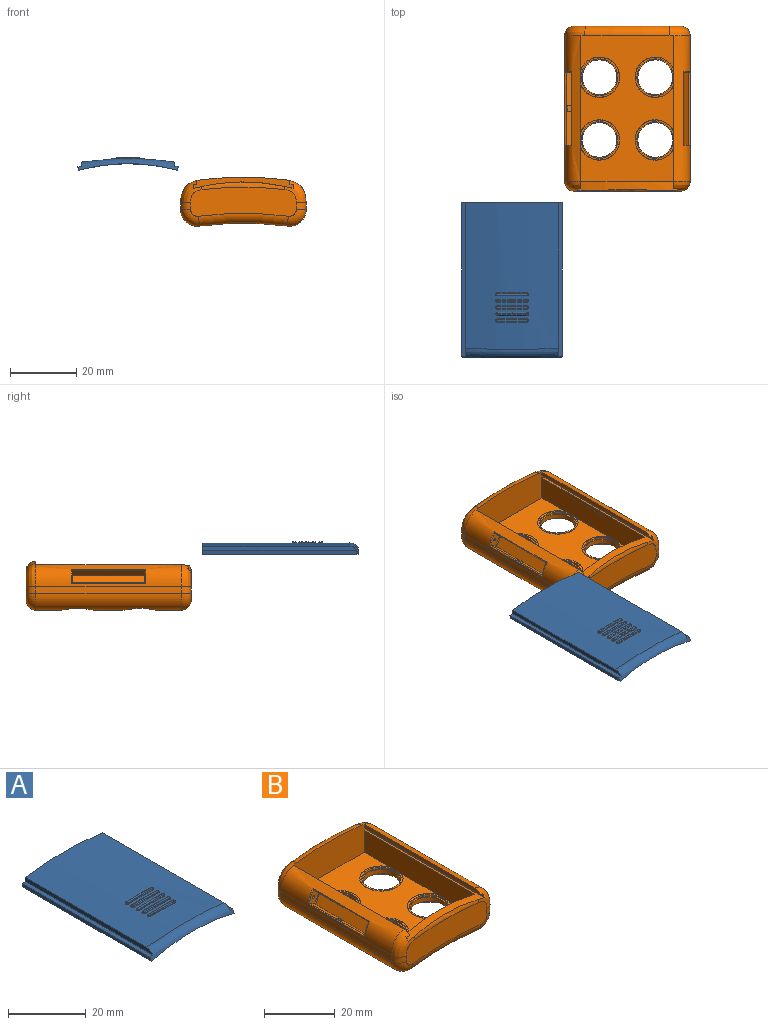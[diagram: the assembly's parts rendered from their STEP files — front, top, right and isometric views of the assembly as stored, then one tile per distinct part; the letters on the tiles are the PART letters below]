
ASSEMBLY  parts=2 mates=1
PART A: 107 faces, bbox 33.4x47.1x4.3 mm
  f0: plane 30.4x3.48mm, normal (0,1,0), area 31.7mm2, adj f1,f2,f3,f4,f5,f6,f7,f8
  f1: cylinder r=58.25mm len=47mm, axis (0,-1,0), area 297.3mm2, adj f0,f2,f8,f9,f10,f105,f106
  f2: plane 47.03x1.14mm, normal (0.99,0,-0.13), area 52.1mm2, adj f0,f1,f3,f9
  f3: plane 46.53x1.1mm, normal (0.13,0,0.99), area 51.7mm2, adj f0,f2,f4,f9
  f4: plane 46.64x1.34mm, normal (1,0,0), area 56.4mm2, adj f0,f3,f5,f9
  f5: cylinder r=99.82mm len=44.4mm, axis (0,-1,0), area 1204.5mm2, adj f0,f4,f6,f9,f13,f14,f15,f16
  f6: plane 46.64x1.35mm, normal (-1,0,0), area 56.4mm2, adj f0,f5,f7,f9
  f7: plane 46.53x1.1mm, normal (-0.13,0,0.99), area 51.7mm2, adj f0,f6,f8,f9
  f8: plane 47.03x1.13mm, normal (-0.99,0,-0.13), area 52.1mm2, adj f0,f1,f7,f9
  f9: bspline ~33.25x3.8mm, area 98.9mm2, adj f1,f2,f3,f4,f5,f6,f7,f8
  f10: plane 26.16x1.86mm, normal (0,1,0), area 19.6mm2, adj f1,f11,f105,f106
  f11: plane 43x20.61mm, normal (0,0,-1), area 886.4mm2, adj f0,f10,f105,f106
  f12: cylinder r=99.82mm len=9.62mm, axis (0,-1,0), area 5.7mm2, adj f95,f96,f97,f98,f99,f100,f101,f102
  f13: cylinder r=0.5mm len=0.1mm, axis (0,0,-1), area 0mm2, adj f5,f14,f21,f99
  f14: cylinder r=0.5mm len=0.1mm, axis (0,0,-1), area 0mm2, adj f5,f13,f15,f97
  f15: plane 4.46x0.2mm, normal (0,-1,0), area 0.4mm2, adj f5,f14,f16,f95
  f16: cylinder r=0.5mm len=1mm, axis (0,0,-1), area 0.2mm2, adj f5,f15,f17,f96
  f17: plane 4.46x0.2mm, normal (0,1,0), area 0.4mm2, adj f5,f16,f18,f98
  f18: cylinder r=0.5mm len=0.1mm, axis (0,0,-1), area 0mm2, adj f5,f17,f19,f100
  f19: cylinder r=0.5mm len=0.1mm, axis (0,0,-1), area 0mm2, adj f5,f18,f20,f102
  f20: plane 4.46x0.2mm, normal (0,1,0), area 0.4mm2, adj f5,f19,f22,f104
  f21: plane 4.46x0.2mm, normal (0,-1,0), area 0.4mm2, adj f5,f13,f22,f101
  f22: cylinder r=0.5mm len=1mm, axis (0,0,-1), area 0.2mm2, adj f5,f20,f21,f103
  f23: cylinder r=99.82mm len=9.56mm, axis (0,-1,0), area 5.7mm2, adj f85,f86,f87,f88,f89,f90,f91,f92
  f24: cylinder r=0.5mm len=0.1mm, axis (0,0,-1), area 0mm2, adj f5,f25,f32,f89
  f25: cylinder r=0.5mm len=0.1mm, axis (0,0,-1), area 0mm2, adj f5,f24,f26,f87
  f26: plane 4.46x0.2mm, normal (0,1,0), area 0.4mm2, adj f5,f25,f27,f85
  f27: cylinder r=0.5mm len=1mm, axis (0,0,-1), area 0.2mm2, adj f5,f26,f28,f86
  f28: plane 4.46x0.2mm, normal (0,-1,0), area 0.4mm2, adj f5,f27,f29,f88
  f29: cylinder r=0.5mm len=0.1mm, axis (0,0,-1), area 0mm2, adj f5,f28,f30,f90
  f30: cylinder r=0.5mm len=0.1mm, axis (0,0,-1), area 0mm2, adj f5,f29,f31,f92
  f31: plane 4.46x0.2mm, normal (0,-1,0), area 0.4mm2, adj f5,f30,f33,f94
  f32: plane 4.46x0.2mm, normal (0,1,0), area 0.4mm2, adj f5,f24,f33,f91
  f33: cylinder r=0.5mm len=1mm, axis (0,0,-1), area 0.2mm2, adj f5,f31,f32,f93
  f34: cylinder r=99.82mm len=8.93mm, axis (0,-1,0), area 5.4mm2, adj f61,f62,f63,f64
  f35: cylinder r=0.5mm len=1mm, axis (0,0,-1), area 0.2mm2, adj f5,f36,f37,f62
  f36: plane 8.92x0.2mm, normal (0,-1,0), area 0.9mm2, adj f5,f35,f38,f64
  f37: plane 8.92x0.2mm, normal (0,1,0), area 0.9mm2, adj f5,f35,f38,f61
  f38: cylinder r=0.5mm len=1mm, axis (0,0,-1), area 0.2mm2, adj f5,f36,f37,f63
  f39: cylinder r=99.82mm len=9.58mm, axis (0,-1,0), area 5.7mm2, adj f75,f76,f77,f78,f79,f80,f81,f82
  f40: cylinder r=0.5mm len=0.1mm, axis (0,0,-1), area 0mm2, adj f5,f41,f48,f79
  f41: cylinder r=0.5mm len=0.1mm, axis (0,0,-1), area 0mm2, adj f5,f40,f42,f77
  f42: plane 4.46x0.2mm, normal (0,1,0), area 0.4mm2, adj f5,f41,f43,f75
  f43: cylinder r=0.5mm len=1mm, axis (0,0,-1), area 0.2mm2, adj f5,f42,f44,f76
  f44: plane 4.46x0.2mm, normal (0,-1,0), area 0.4mm2, adj f5,f43,f45,f78
  f45: cylinder r=0.5mm len=0.1mm, axis (0,0,-1), area 0mm2, adj f5,f44,f46,f80
  f46: cylinder r=0.5mm len=0.1mm, axis (0,0,-1), area 0mm2, adj f5,f45,f47,f82
  f47: plane 4.46x0.2mm, normal (0,-1,0), area 0.4mm2, adj f5,f46,f49,f84
  f48: plane 4.46x0.2mm, normal (0,1,0), area 0.4mm2, adj f5,f40,f49,f81
  f49: cylinder r=0.5mm len=1mm, axis (0,0,-1), area 0.2mm2, adj f5,f47,f48,f83
  f50: cylinder r=99.82mm len=9.6mm, axis (0,-1,0), area 5.7mm2, adj f65,f66,f67,f68,f69,f70,f71,f72
  f51: cylinder r=0.5mm len=0.1mm, axis (0,0,-1), area 0mm2, adj f5,f52,f59,f69
  f52: cylinder r=0.5mm len=0.1mm, axis (0,0,-1), area 0mm2, adj f5,f51,f53,f67
  f53: plane 4.46x0.2mm, normal (0,1,0), area 0.4mm2, adj f5,f52,f54,f65
  f54: cylinder r=0.5mm len=1mm, axis (0,0,-1), area 0.2mm2, adj f5,f53,f55,f66
  f55: plane 4.46x0.2mm, normal (0,-1,0), area 0.4mm2, adj f5,f54,f56,f68
  f56: cylinder r=0.5mm len=0.1mm, axis (0,0,-1), area 0mm2, adj f5,f55,f57,f70
  f57: cylinder r=0.5mm len=0.1mm, axis (0,0,-1), area 0mm2, adj f5,f56,f58,f72
  f58: plane 4.46x0.2mm, normal (0,-1,0), area 0.4mm2, adj f5,f57,f60,f74
  f59: plane 4.46x0.2mm, normal (0,1,0), area 0.4mm2, adj f5,f51,f60,f71
  f60: cylinder r=0.5mm len=1mm, axis (0,0,-1), area 0.2mm2, adj f5,f58,f59,f73
  f61: torus R=99.62mm, axis (0,1,0), area 2.8mm2, adj f34,f37,f62,f63
  f62: bspline ~1x0.61mm, area 0.4mm2, adj f34,f35,f61,f64
  f63: bspline ~1x0.61mm, area 0.4mm2, adj f34,f38,f61,f64
  f64: torus R=99.62mm, axis (0,1,0), area 2.8mm2, adj f34,f36,f62,f63
  f65: torus R=99.62mm, axis (0,-1,0), area 1.4mm2, adj f50,f53,f66,f67
  f66: bspline ~1x0.61mm, area 0.4mm2, adj f50,f54,f65,f68
  f67: bspline ~0.21x0.2mm, area 0mm2, adj f50,f52,f65,f69
  f68: torus R=99.62mm, axis (0,-1,0), area 1.4mm2, adj f50,f55,f66,f70
  f69: bspline ~0.21x0.2mm, area 0mm2, adj f50,f51,f67,f71
  f70: bspline ~0.21x0.2mm, area 0mm2, adj f50,f56,f68,f72
  f71: torus R=99.62mm, axis (0,1,0), area 1.4mm2, adj f50,f59,f69,f73
  f72: bspline ~0.21x0.2mm, area 0mm2, adj f50,f57,f70,f74
  f73: bspline ~1x0.61mm, area 0.4mm2, adj f50,f60,f71,f74
  f74: torus R=99.62mm, axis (0,1,0), area 1.4mm2, adj f50,f58,f72,f73
  f75: torus R=99.62mm, axis (0,-1,0), area 1.4mm2, adj f39,f42,f76,f77
  f76: bspline ~1x0.61mm, area 0.4mm2, adj f39,f43,f75,f78
  f77: bspline ~0.21x0.2mm, area 0mm2, adj f39,f41,f75,f79
  f78: torus R=99.62mm, axis (0,-1,0), area 1.4mm2, adj f39,f44,f76,f80
  f79: bspline ~0.21x0.2mm, area 0mm2, adj f39,f40,f77,f81
  f80: bspline ~0.21x0.2mm, area 0mm2, adj f39,f45,f78,f82
  f81: torus R=99.62mm, axis (0,1,0), area 1.4mm2, adj f39,f48,f79,f83
  f82: bspline ~0.21x0.2mm, area 0mm2, adj f39,f46,f80,f84
  f83: bspline ~1x0.61mm, area 0.4mm2, adj f39,f49,f81,f84
  f84: torus R=99.62mm, axis (0,1,0), area 1.4mm2, adj f39,f47,f82,f83
  f85: torus R=99.62mm, axis (0,-1,0), area 1.4mm2, adj f23,f26,f86,f87
  f86: bspline ~1x0.61mm, area 0.4mm2, adj f23,f27,f85,f88
  f87: bspline ~0.21x0.2mm, area 0mm2, adj f23,f25,f85,f89
  f88: torus R=99.62mm, axis (0,-1,0), area 1.4mm2, adj f23,f28,f86,f90
  f89: bspline ~0.21x0.2mm, area 0mm2, adj f23,f24,f87,f91
  f90: bspline ~0.21x0.2mm, area 0mm2, adj f23,f29,f88,f92
  f91: torus R=99.62mm, axis (0,1,0), area 1.4mm2, adj f23,f32,f89,f93
  f92: bspline ~0.21x0.2mm, area 0mm2, adj f23,f30,f90,f94
  f93: bspline ~1x0.61mm, area 0.4mm2, adj f23,f33,f91,f94
  f94: torus R=99.62mm, axis (0,1,0), area 1.4mm2, adj f23,f31,f92,f93
  f95: torus R=99.62mm, axis (0,1,0), area 1.4mm2, adj f12,f15,f96,f97
  f96: bspline ~1x0.61mm, area 0.4mm2, adj f12,f16,f95,f98
  f97: bspline ~0.21x0.2mm, area 0mm2, adj f12,f14,f95,f99
  f98: torus R=99.62mm, axis (0,1,0), area 1.4mm2, adj f12,f17,f96,f100
  f99: bspline ~0.21x0.2mm, area 0mm2, adj f12,f13,f97,f101
  f100: bspline ~0.21x0.2mm, area 0mm2, adj f12,f18,f98,f102
  f101: torus R=99.62mm, axis (0,-1,0), area 1.4mm2, adj f12,f21,f99,f103
  f102: bspline ~0.21x0.2mm, area 0mm2, adj f12,f19,f100,f104
  f103: bspline ~1x0.61mm, area 0.4mm2, adj f12,f22,f101,f104
  f104: torus R=99.62mm, axis (0,-1,0), area 1.4mm2, adj f12,f20,f102,f103
  f105: cylinder r=3mm len=43mm, axis (0,-1,0), area 152.3mm2, adj f0,f1,f10,f11
  f106: cylinder r=3mm len=43mm, axis (0,-1,0), area 151.7mm2, adj f0,f1,f10,f11
PART B: 101 faces, bbox 38.2x55.2x16 mm
  f0: plane 44x7.47mm, normal (1,0,0), area 326.3mm2, adj f6,f11,f24,f82,f83,f84,f85,f90
  f1: plane 22.15x2.02mm, normal (0.55,0,0.84), area 49.9mm2, adj f2,f15,f26,f29,f30,f77,f95,f96
  f2: plane 21.75x3.38mm, normal (-0.84,0,0.55), area 87.3mm2, adj f1,f25,f29,f30,f95,f96,f97
  f3: plane 46.55x1.38mm, normal (1,0,0), area 53.5mm2, adj f7,f18,f24,f93
  f4: plane 46.55x1.38mm, normal (-1,0,0), area 53.5mm2, adj f14,f24,f36,f92
  f5: plane 44x7.47mm, normal (-1,0,0), area 328.5mm2, adj f6,f11,f24,f66,f67,f68,f69,f90
  f6: plane 28.2x9.2mm, normal (0,1,0), area 243.3mm2, adj f0,f5,f11,f90
  f7: bspline ~10.48x9.59mm, area 34.9mm2, adj f3,f8,f18,f22,f33,f90,f93,f94
  f8: torus R=96.82mm, axis (0,-1,0), area 34.4mm2, adj f7,f22,f36,f90
  f9: cylinder r=5.25mm len=10.5mm, axis (0,0,-1), area 49.5mm2, adj f52,f88
  f10: cylinder r=5.25mm len=10.5mm, axis (0,0,-1), area 49.5mm2, adj f50,f87
  f11: plane 44x28.83mm, normal (0,0,1), area 776.2mm2, adj f0,f5,f6,f24,f66,f69,f83,f84
  f12: cylinder r=5.25mm len=10.5mm, axis (0,0,-1), area 49.5mm2, adj f48,f81
  f13: cylinder r=5.25mm len=10.5mm, axis (0,0,-1), area 49.5mm2, adj f46,f78
  f14: bspline ~55x6.94mm, area 290mm2, adj f4,f20,f36,f44,f70,f71,f72,f73
  f15: plane 4.98x4.16mm, normal (0,1,0), area 11mm2, adj f1,f25,f30,f54,f74,f75,f77
  f16: cylinder r=100mm len=44mm, axis (0,1,0), area 505.2mm2, adj f17,f19,f32,f39,f45,f47,f49,f51
  f17: cylinder r=5.08mm len=44mm, axis (0,1,0), area 328.4mm2, adj f16,f21,f31,f37,f49,f51
  f18: bspline ~55x6.94mm, area 290mm2, adj f3,f7,f21,f40,f74,f75,f76,f77
  f19: cylinder r=5.08mm len=44mm, axis (0,1,0), area 342.8mm2, adj f16,f20,f34,f41,f45,f47
  f20: plane 44x2.05mm, normal (1,0,0), area 90mm2, adj f14,f19,f35,f43
  f21: plane 44x2.05mm, normal (-1,0,0), area 90mm2, adj f17,f18,f33,f38
  f22: plane 32x8.91mm, normal (0,-1,0), area 248.6mm2, adj f7,f8,f31,f32,f33,f34,f35,f36
  f23: plane 32x8.91mm, normal (0,1,0), area 248.6mm2, adj f37,f38,f39,f40,f41,f42,f43,f44
  f24: plane 30.46x10.75mm, normal (0,-1,0), area 294.5mm2, adj f0,f3,f4,f5,f11,f40,f42,f44
  f25: plane 22.15x2.55mm, normal (-0.55,0,-0.84), area 67.4mm2, adj f2,f15,f26,f29,f30,f74
  f26: plane 4.96x4.16mm, normal (0,-1,0), area 10.9mm2, adj f1,f25,f28,f29,f74,f76,f77
  f27: cone r=0mm half-angle=59deg, axis (0,-1,0), area 0.6mm2, adj f28
  f28: cylinder r=0.41mm len=2mm, axis (0,-1,0), area 5.2mm2, adj f26,f27
  f29: cylinder r=0.2mm len=3.46mm, axis (0.55,0,0.84), area 1.3mm2, adj f1,f2,f25,f26
  f30: cylinder r=0.2mm len=3.49mm, axis (-0.55,0,-0.84), area 1.3mm2, adj f1,f2,f15,f25
  f31: torus R=2.08mm, axis (0,-1,0), area 32mm2, adj f17,f22,f32,f33
  f32: torus R=103mm, axis (0,-1,0), area 126.6mm2, adj f16,f22,f31,f34
  f33: cylinder r=3mm len=3mm, axis (0,0,1), area 9.6mm2, adj f7,f21,f22,f31
  f34: torus R=2.08mm, axis (0,-1,0), area 32mm2, adj f19,f22,f32,f35
  f35: cylinder r=3mm len=3mm, axis (0,0,-1), area 9.6mm2, adj f20,f22,f34,f36
  f36: bspline ~10.48x9.59mm, area 34.6mm2, adj f4,f8,f14,f22,f35,f90,f91,f92
  f37: torus R=2.08mm, axis (0,-1,0), area 32mm2, adj f17,f23,f38,f39
  f38: cylinder r=3mm len=3mm, axis (0,0,-1), area 9.6mm2, adj f21,f23,f37,f40
  f39: torus R=103mm, axis (0,-1,0), area 126.6mm2, adj f16,f23,f37,f41
  f40: bspline ~10.48x9.59mm, area 41.2mm2, adj f18,f23,f24,f38,f42
  f41: torus R=2.08mm, axis (0,-1,0), area 32mm2, adj f19,f23,f39,f43
  f42: torus R=96.82mm, axis (0,-1,0), area 120.6mm2, adj f23,f24,f40,f44
  f43: cylinder r=3mm len=3mm, axis (0,0,1), area 9.6mm2, adj f20,f23,f41,f44
  f44: bspline ~10.48x9.59mm, area 41.2mm2, adj f14,f23,f24,f42,f43
  f45: cylinder r=7.8mm len=15.6mm, axis (0,0,1), area 75.7mm2, adj f16,f19,f46
  f46: plane 15.6x15.6mm, normal (0,0,-1), area 104.5mm2, adj f13,f45
  f47: cylinder r=7.8mm len=15.6mm, axis (0,0,1), area 75.7mm2, adj f16,f19,f48
  f48: plane 15.6x15.6mm, normal (0,0,-1), area 104.5mm2, adj f12,f47
  f49: cylinder r=7.8mm len=15.6mm, axis (0,0,1), area 101.6mm2, adj f16,f17,f50
  f50: plane 15.6x15.6mm, normal (0,0,-1), area 104.5mm2, adj f10,f49
  f51: cylinder r=7.8mm len=15.6mm, axis (0,0,1), area 101.6mm2, adj f16,f17,f52
  f52: plane 15.6x15.6mm, normal (0,0,-1), area 104.5mm2, adj f9,f51
  f53: cone r=0mm half-angle=59deg, axis (0,1,0), area 0.6mm2, adj f54
  f54: cylinder r=0.41mm len=2mm, axis (0,1,0), area 5.2mm2, adj f15,f53
  f55: plane 4.98x4.16mm, normal (0,1,0), area 11mm2, adj f57,f58,f63,f65,f70,f71,f73
  f56: plane 4.96x4.16mm, normal (0,-1,0), area 10.9mm2, adj f57,f58,f61,f62,f70,f72,f73
  f57: plane 22.15x2.55mm, normal (0.55,0,-0.84), area 67.4mm2, adj f55,f56,f59,f62,f63,f70
  f58: plane 22.15x2.02mm, normal (-0.55,0,0.84), area 53.3mm2, adj f55,f56,f59,f62,f63,f73
  f59: plane 21.75x3.38mm, normal (0.84,0,0.55), area 87.4mm2, adj f57,f58,f62,f63
  f60: cone r=0mm half-angle=59deg, axis (0,-1,0), area 0.6mm2, adj f61
  f61: cylinder r=0.41mm len=2mm, axis (0,-1,0), area 5.2mm2, adj f56,f60
  f62: cylinder r=0.2mm len=3.46mm, axis (0.55,0,-0.84), area 1.3mm2, adj f56,f57,f58,f59
  f63: cylinder r=0.2mm len=3.49mm, axis (-0.55,0,0.84), area 1.3mm2, adj f55,f57,f58,f59
  f64: cone r=0mm half-angle=59deg, axis (0,1,0), area 0.6mm2, adj f65
  f65: cylinder r=0.41mm len=2mm, axis (0,1,0), area 5.2mm2, adj f55,f64
  f66: cone r=6.05mm half-angle=80deg, axis (0,0,-1), area 2.6mm2, adj f5,f11,f67
  f67: plane 12.1x11.71mm, normal (0,0,1), area 17.1mm2, adj f5,f66,f80
  f68: plane 12.1x11.71mm, normal (0,0,1), area 17.1mm2, adj f5,f69,f79
  f69: cone r=6.05mm half-angle=80deg, axis (0,0,-1), area 2.6mm2, adj f5,f11,f68
  f70: cylinder r=0.25mm len=22.65mm, axis (0,1,0), area 10.4mm2, adj f14,f55,f56,f57,f71,f72
  f71: bspline ~5.36x3.02mm, area 1.8mm2, adj f14,f55,f70,f73
  f72: bspline ~5.35x3.03mm, area 1.8mm2, adj f14,f56,f70,f73
  f73: bspline ~43.42x0.47mm, area 11.5mm2, adj f14,f55,f56,f58,f71,f72
  f74: cylinder r=0.25mm len=22.65mm, axis (0,1,0), area 10.4mm2, adj f15,f18,f25,f26,f75,f76
  f75: bspline ~5.36x3.02mm, area 1.8mm2, adj f15,f18,f74,f77
  f76: bspline ~5.35x3.03mm, area 1.8mm2, adj f18,f26,f74,f77
  f77: bspline ~43.42x0.47mm, area 11.5mm2, adj f1,f15,f18,f26,f75,f76
  f78: plane 11.1x11.1mm, normal (0,0,1), area 10.2mm2, adj f13,f79
  f79: cylinder r=5.55mm len=11.1mm, axis (0,0,1), area 20.9mm2, adj f68,f78
  f80: cylinder r=5.55mm len=11.1mm, axis (0,0,1), area 20.9mm2, adj f67,f81
  f81: plane 11.1x11.1mm, normal (0,0,1), area 10.2mm2, adj f12,f80
  f82: plane 12.1x11.71mm, normal (0,0,1), area 17.1mm2, adj f0,f83,f89
  f83: cone r=6.05mm half-angle=80deg, axis (0,0,-1), area 2.6mm2, adj f0,f11,f82
  f84: cone r=6.05mm half-angle=80deg, axis (0,0,-1), area 2.6mm2, adj f0,f11,f85
  f85: plane 12.1x11.71mm, normal (0,0,1), area 17.1mm2, adj f0,f84,f86
  f86: cylinder r=5.55mm len=11.1mm, axis (0,0,1), area 20.9mm2, adj f85,f87
  f87: plane 11.1x11.1mm, normal (0,0,1), area 10.2mm2, adj f10,f86
  f88: plane 11.1x11.1mm, normal (0,0,1), area 10.2mm2, adj f9,f89
  f89: cylinder r=5.55mm len=11.1mm, axis (0,0,1), area 20.9mm2, adj f82,f88
  f90: cylinder r=58.25mm len=46.85mm, axis (0,-1,0), area 173.8mm2, adj f0,f5,f6,f7,f8,f24,f36,f91
  f91: plane 46.86x1.16mm, normal (-0.99,0,0.13), area 51.8mm2, adj f24,f36,f90,f92
  f92: plane 46.44x1.19mm, normal (-0.13,0,-0.99), area 51.4mm2, adj f4,f24,f36,f91
  f93: plane 46.44x1.19mm, normal (0.13,0,-0.99), area 51.4mm2, adj f3,f7,f24,f94
  f94: plane 46.86x1.16mm, normal (0.99,0,0.13), area 51.8mm2, adj f7,f24,f90,f93
  f95: plane 4.34x3.93mm, normal (0,-1,0), area 6.9mm2, adj f0,f1,f2,f11,f97,f98,f99,f100
  f96: plane 4.34x3.93mm, normal (0,1,0), area 6.9mm2, adj f0,f1,f2,f11,f97,f98,f99,f100
  f97: plane 2.44x1.7mm, normal (-0.55,0,-0.84), area 5mm2, adj f0,f2,f95,f96
  f98: plane 3.41x2.23mm, normal (0.55,0,0.84), area 6.9mm2, adj f11,f95,f96,f100
  f99: plane 1.7x0.32mm, normal (0.84,0,-0.55), area 0.7mm2, adj f1,f95,f96,f100
  f100: plane 1.7x1.38mm, normal (0.98,0,0.21), area 2.4mm2, adj f95,f96,f98,f99
PLACE A t=(13.24,-92.92,-21.98)mm
PLACE B t=(48.17,-42.36,-27.51)mm
MATE parallel A.f2 <-> B.f91  axis (0.99,0,-0.13) through (47.37,-119.31,-15.09)mm
